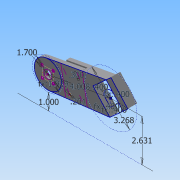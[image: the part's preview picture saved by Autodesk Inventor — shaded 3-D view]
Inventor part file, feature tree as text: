
AUTODESK INVENTOR PART (.ipt)
format: ipt  version: 2014 SP1 (Build 180222100, 222)  size: 258,560 bytes
history: native  units: in
note: dims shown in document units (in); Inventor stores cm internally (conversion verified against a paired STEP export)
features: other x16, extrude x7, fillet x4, sketch x3, hole x2, pattern_linear x1
ambient origin geometry x8: Origin, YZ Plane, XZ Plane, XY Plane, X Axis, Y Axis, Z Axis, Center Point
bodies: Solid4 (feature_tree), Solid6 (feature_tree)
feature tree (33):
  other  "MountV4"
  other  "Blocks"
  other  "Base Sketch"
  extrude  "Base"  Depth=0.4in
  extrude  "Extrusion7"  Depth=0.4in
  extrude  "Extrusion8"  Depth=0.25in TaperAngle=0.0deg
  other  "Motor Hole Sketch"
  extrude  "Motor Hole"  [1 undecoded]
  extrude  "Motor Cbore"  Depth=0.25in
  pattern_linear  "Rectangular Pattern1"  Spacing1=0.0in  [1 undecoded]
  extrude  "Motor Axle"  Depth=0.25in
  other  "Back Plane"
  extrude  "Pocket"  Depth=0.25in
  other  "Midplane"
  sketch  "Sketch15"  dims[d98=0.4in d99=0.4in]
  sketch  "Sketch16"  dims[d116=0.0in d130=0.5in d131=0.0in d134=-0.6in d135=0.4125in d136=0.0in d153=0.25in d155=0.125in d157=1.7in d158=0.3in d168=0.337in d167=-0.3in d176=0.3in d177=0.3in d178=0.3in d179=0.6323in d180=0.6323in d182=0.125in d183=0.25in d186=0.6066in d187=0.6066in d188=0.09in d189=0.9843in d192=0.4882in d193=0.1772in d195=0.3543in d197=0.9843in d211=0.4252in d212=0.7874in d214=0.6955in d215=0.7874in d217=0.6955in d218=0.3543in d219=0.1181in d220=0.0in d221=0.1181in d222=0.0in d226=0.25in d228=1.9291in d229=0.1in d231=0.78in d233=1.9291in d235=0.3in d236=0.3in d237=0.104in d238=0.75in d239=0.375in d240=0.25in d241=0.5635in d242=1.0in d243=0.8108in d244=0.104in d245=0.75in d246=0.375in d247=0.25in d248=0.5635in d249=1.0in d250=0.8108in d251=0.25in d252=0.1in d258=0.3in d261=0.35in d262=0.0in d263=0.25in d264=0.0in d169=1.0in]
  hole  "Hole3"  [1 undecoded]
  hole  "Hole4"  [1 undecoded]
  fillet  "Fillet1"  [1 undecoded]
  fillet  "Fillet2"  Radius=0.3in
  fillet  "Fillet3"  Radius=0.3in
  fillet  "Fillet4"  Radius=0.6323in
  other  "the Axle"
  other  "Motor Mount Pattern"
  sketch  "Sketch12"  dims[d84=0.715in d85=0.9482in d97=0.4in]
  other  "Motor Body Extent"
  other  "Block7"
  other  "MotorMountPattern"
  other  "AxleOutline"
  other  "Motor Mount Pattern:4"
  other  "Motor Mount Pattern:5"
  other  "Motor Mount Pattern:6"
  other  "MotorMountPattern:1"
note: 5 required parameter values undecoded (feature->parameter linkage not recoverable at this tier; creation-order binding heuristic only, values carry confidence <= 0.55)
